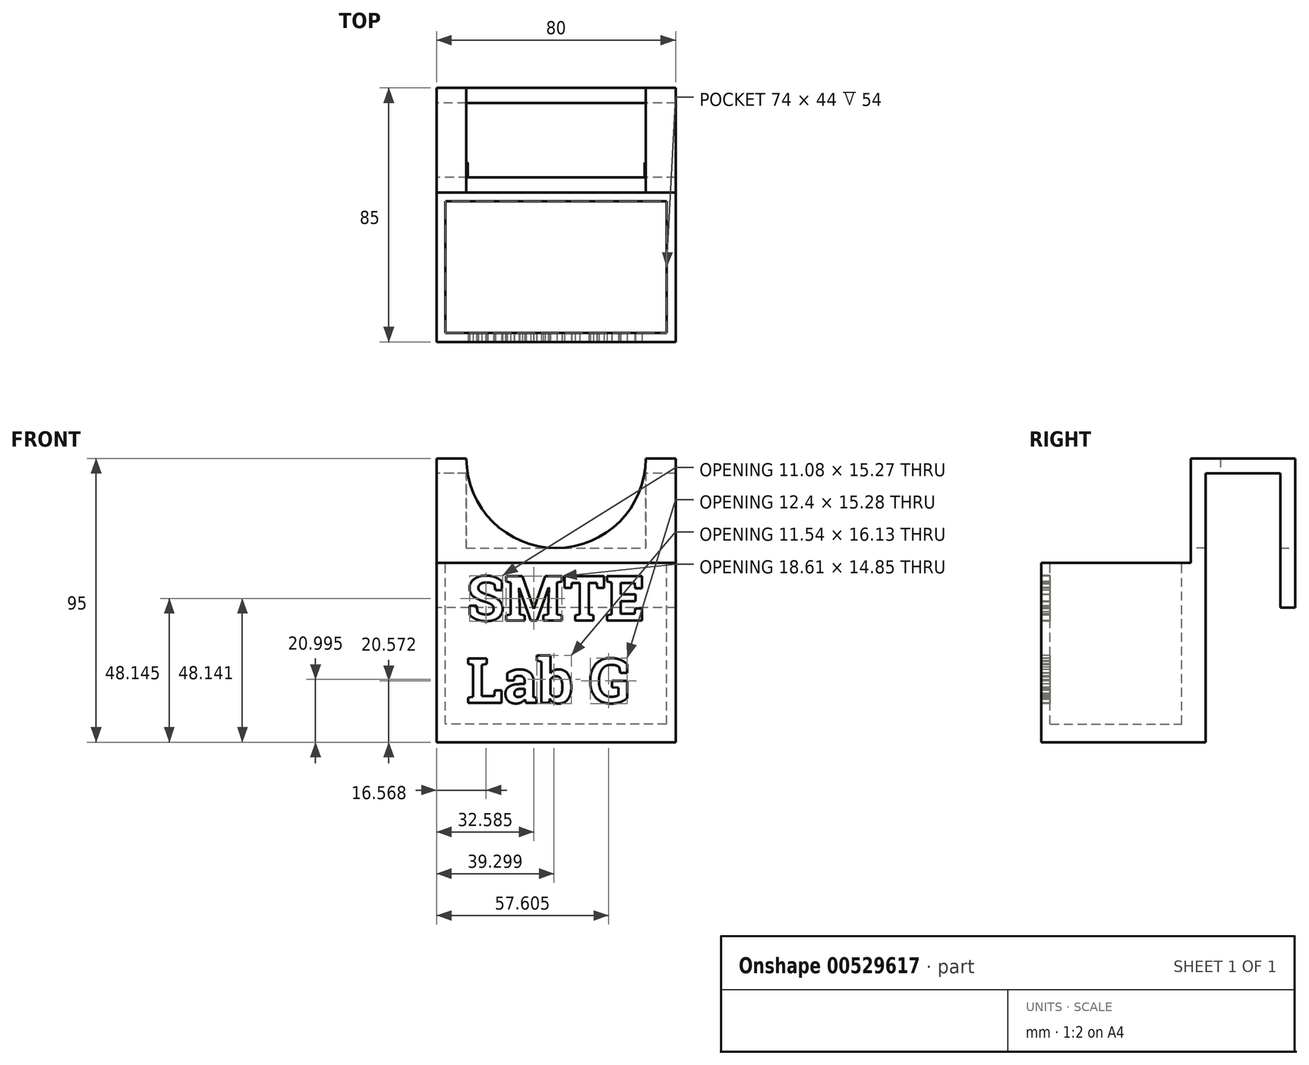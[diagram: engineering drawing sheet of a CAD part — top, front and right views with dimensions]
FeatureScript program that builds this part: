
annotation { "Feature Type Name" : "Feature", "Feature Type Description" : "" }
export const myFeature = defineFeature(function(context is Context, id is Id, definition is map)
    precondition{}
    {
        {
            var Q0;
            Q0=qCreatedBy(makeId("Right.planeOp"),FACE);
            var sketch = newSketch(context, id + "F0", { "sketchPlane" : qUnion([Q0])});
            skLineSegment(sketch, "E0.bottom", {"start": v(0, 0) * mm, "end": v(-55, 0) * mm});
            skLineSegment(sketch, "E0.top", {"start": v(-5, 60) * mm, "end": v(-55, 60) * mm});
            skLineSegment(sketch, "E0.left", {"start": v(0, 0) * mm, "end": v(0, 60) * mm});
            skLineSegment(sketch, "E0.right", {"start": v(-55, 0) * mm, "end": v(-55, 60) * mm});
            skLineSegment(sketch, "E1", {"start": v(-5, 60) * mm, "end": v(-5, 95) * mm});
            skLineSegment(sketch, "E2", {"start": v(-5, 95) * mm, "end": v(30, 95) * mm});
            skLineSegment(sketch, "E3", {"start": v(30, 95) * mm, "end": v(30, 45) * mm});
            skLineSegment(sketch, "E4", {"start": v(30, 45) * mm, "end": v(25, 45) * mm});
            skLineSegment(sketch, "E5", {"start": v(25, 45) * mm, "end": v(25, 90) * mm});
            skLineSegment(sketch, "E6", {"start": v(25, 90) * mm, "end": v(0, 90) * mm});
            skLineSegment(sketch, "E7", {"start": v(0, 90) * mm, "end": v(0, 60) * mm});
            skPoint(sketch, "E8.orphan", {"position": v(-5, 35) * mm});
            skSolve(sketch);
        }
        {
            var Q0;
            Q0=makeQuery(id+"F0.imprint","IMPRINT",FACE,{"disambiguationData":[TD([[makeQuery(id+"F0.imprint","IMPRINT",EDGE,{"derivedFrom":sQuery(id+"F0.wireOp",EDGE,"E0.bottom")}),-1.0]])]});
            extrude(context, id + "F1", {"entities" : qUnion([Q0]), "depth" : 80 * mm, "offsetDistance" : 25 * mm});
        }
        {
            var Q0;
            Q0=makeQuery(id+"F1.opExtrude","SWEPT_FACE",FACE,{"disambiguationData":[OSD([sQuery(id+"F0.wireOp",EDGE,"E0.top")])]});
            var sketch = newSketch(context, id + "F2", { "sketchPlane" : qUnion([Q0])});
            skLineSegment(sketch, "E9.bottom", {"start": v(77, -52) * mm, "end": v(3, -52) * mm});
            skLineSegment(sketch, "E9.top", {"start": v(77, -8) * mm, "end": v(3, -8) * mm});
            skLineSegment(sketch, "E9.left", {"start": v(77, -52) * mm, "end": v(77, -8) * mm});
            skLineSegment(sketch, "E9.right", {"start": v(3, -52) * mm, "end": v(3, -8) * mm});
            skPoint(sketch, "E9.middle", {"position": v(40, -30) * mm});
            skPoint(sketch, "E10.trimOffspring.end.orphan", {"position": v(80, -55) * mm});
            skPoint(sketch, "E11.start.orphan", {"position": v(0, -5) * mm});
            skSolve(sketch);
        }
        {
            var Q0;
            Q0 = qSketchRegion(id + "F2", true);
            extrude(context, id + "F3", {"entities" : qUnion([Q0]), "operationType" : NewBodyOperationType.REMOVE, "oppositeDirection" : true, "depth" : 54 * mm, "offsetDistance" : 25 * mm});
        }
        {
            var Q0;
            Q0=makeQuery(id+"F1.opExtrude","SWEPT_FACE",FACE,{"disambiguationData":[OSD([sQuery(id+"F0.wireOp",EDGE,"E1")])]});
            var sketch = newSketch(context, id + "F4", { "sketchPlane" : qUnion([Q0])});
            skArc(sketch, "E12", {"start": v(10, 95) * mm, "mid": v(40, 65) * mm, "end": v(70, 95) * mm});
            skPoint(sketch, "E13.start.orphan", {"position": v(40, 77.5) * mm});
            skPoint(sketch, "E14.trimOffspring.end.orphan", {"position": v(80, 95) * mm});
            skLineSegment(sketch, "E15", {"start": v(10, 95) * mm, "end": v(70, 95) * mm});
            skPoint(sketch, "E16.start.orphan", {"position": v(0, 60) * mm});
            skSolve(sketch);
        }
        {
            var Q0;
            Q0 = qSketchRegion(id + "F4", true);
            extrude(context, id + "F5", {"entities" : qUnion([Q0]), "operationType" : NewBodyOperationType.REMOVE, "endBound" : BoundingType.THROUGH_ALL, "oppositeDirection" : true, "depth" : 25 * mm, "offsetDistance" : 25 * mm});
        }
        {
            var Q0;
            Q0=makeQuery(id+"F1.opExtrude","SWEPT_FACE",FACE,{"disambiguationData":[OSD([sQuery(id+"F0.wireOp",EDGE,"E3")])]});
            var sketch = newSketch(context, id + "F6", { "sketchPlane" : qUnion([Q0])});
            skLineSegment(sketch, "E17", {"start": v(-70, 95) * mm, "end": v(-70, 65) * mm});
            skLineSegment(sketch, "E18", {"start": v(-10, 95) * mm, "end": v(-10, 65) * mm});
            skLineSegment(sketch, "E19", {"start": v(-40, 65) * mm, "end": v(-10, 65) * mm});
            skLineSegment(sketch, "E20", {"start": v(-70, 65) * mm, "end": v(-40, 65) * mm});
            skLineSegment(sketch, "E21", {"start": v(-70, 95) * mm, "end": v(-10, 95) * mm});
            skSolve(sketch);
        }
        {
            var Q0;
            Q0 = qSketchRegion(id + "F6", true);
            extrude(context, id + "F7", {"entities" : qUnion([Q0]), "operationType" : NewBodyOperationType.REMOVE, "oppositeDirection" : true, "depth" : 25 * mm, "offsetDistance" : 25 * mm});
        }
        {
            var Q0;
            Q0=makeQuery(id+"F1.opExtrude","SWEPT_FACE",FACE,{"disambiguationData":[OSD([sQuery(id+"F0.wireOp",EDGE,"E0.right")])]});
            var sketch = newSketch(context, id + "F8", { "sketchPlane" : qUnion([Q0])});
            skText(sketch, "E22", { "text": "SMTE\nLab G", "fontName": "RobotoSlab-Bold.ttf"});
            const initialGuessF8  = {"E22": [0.01004, 0.04072, 1, 0, 0.01504]};
            skSetInitialGuess(sketch, initialGuessF8);
            skSolve(sketch);
        }
        {
            var Q0;
            Q0 = qSketchRegion(id + "F8", true);
            extrude(context, id + "F9", {"entities" : qUnion([Q0]), "operationType" : NewBodyOperationType.REMOVE, "oppositeDirection" : true, "depth" : 4 * mm, "offsetDistance" : 25 * mm});
        }
    });
